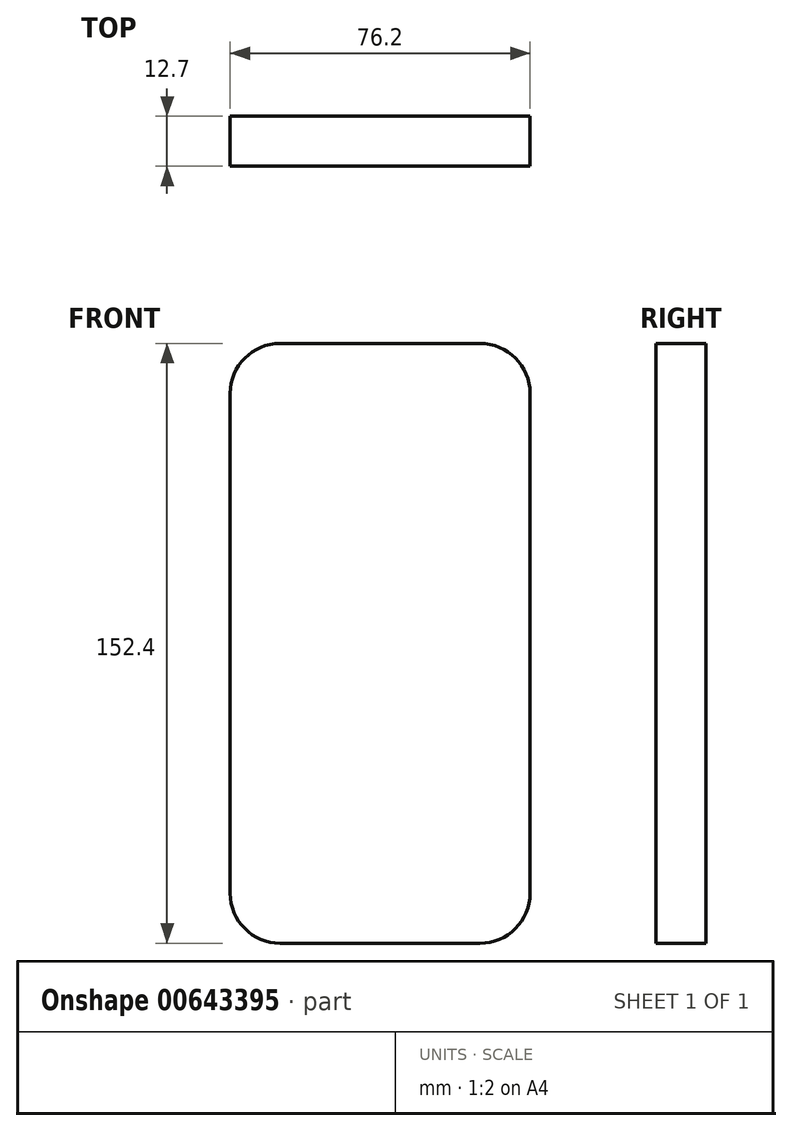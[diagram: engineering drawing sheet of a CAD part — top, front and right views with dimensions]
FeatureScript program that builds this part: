
annotation { "Feature Type Name" : "Feature", "Feature Type Description" : "" }
export const myFeature = defineFeature(function(context is Context, id is Id, definition is map)
    precondition{}
    {
        {
            var Q0;
            Q0=qCreatedBy(makeId("Front.planeOp"),FACE);
            var sketch = newSketch(context, id + "F0", { "sketchPlane" : qUnion([Q0])});
            skLineSegment(sketch, "E0.bottom", {"start": v(0, 0) * mm, "end": v(76.2, 0) * mm});
            skLineSegment(sketch, "E0.top", {"start": v(0, 152.4) * mm, "end": v(76.2, 152.4) * mm});
            skLineSegment(sketch, "E0.left", {"start": v(0, 0) * mm, "end": v(0, 152.4) * mm});
            skLineSegment(sketch, "E0.right", {"start": v(76.2, 0) * mm, "end": v(76.2, 152.4) * mm});
            skSolve(sketch);
        }
        {
            var Q0;
            Q0=makeQuery(id+"F0.imprint","IMPRINT",FACE,{"disambiguationData":[TD([[makeQuery(id+"F0.imprint","IMPRINT",EDGE,{"derivedFrom":sQuery(id+"F0.wireOp",EDGE,"E0.bottom")}),1.0]])]});
            extrude(context, id + "F1", {"entities" : qUnion([Q0]), "depth" : 12.7 * mm, "offsetDistance" : 25.4 * mm});
        }
        {
            var Q0;
            Q0=makeQuery(id+"F1.opExtrude","SWEPT_EDGE",EDGE,{"disambiguationData":[OSD([sQuery(id+"F0.wireOp",EDGE,"E0.bottom"),sQuery(id+"F0.wireOp",EDGE,"E0.right")])]});
            var Q1;
            Q1=makeQuery(id+"F1.opExtrude","SWEPT_EDGE",EDGE,{"disambiguationData":[OSD([sQuery(id+"F0.wireOp",EDGE,"E0.top"),sQuery(id+"F0.wireOp",EDGE,"E0.right")])]});
            var Q2;
            Q2=makeQuery(id+"F1.opExtrude","SWEPT_EDGE",EDGE,{"disambiguationData":[OSD([sQuery(id+"F0.wireOp",EDGE,"E0.top"),sQuery(id+"F0.wireOp",EDGE,"E0.left")])]});
            var Q3;
            Q3=makeQuery(id+"F1.opExtrude","SWEPT_EDGE",EDGE,{"disambiguationData":[OSD([sQuery(id+"F0.wireOp",EDGE,"E0.bottom"),sQuery(id+"F0.wireOp",EDGE,"E0.left")])]});
            fillet(context, id + "F2", {"entities" : qUnion([Q0, Q1, Q2, Q3]), "radius" : 12.7 * mm, "tangentPropagation" : true, "allowEdgeOverflow" : false});
        }
    });
